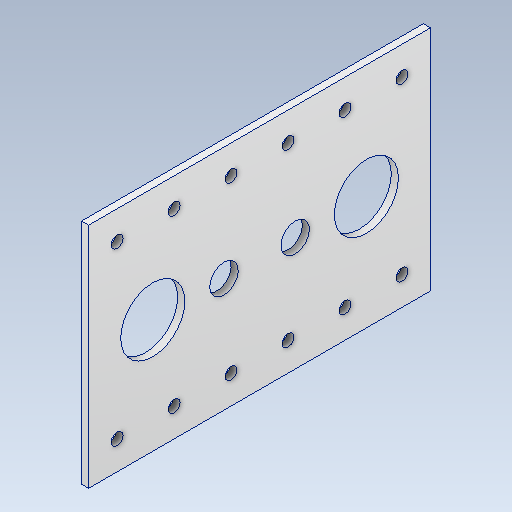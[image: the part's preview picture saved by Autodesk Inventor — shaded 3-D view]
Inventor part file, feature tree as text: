
AUTODESK INVENTOR PART (.ipt)
format: ipt  version: 2023 (Build 270158000, 158)  size: 138,240 bytes
history: native  units: in
note: dims shown in document units (in); Inventor stores cm internally (conversion verified against a paired STEP export)
features: other x3, sketch x1
ambient origin geometry x8: Origin, YZ Plane, XZ Plane, XY Plane, X Axis, Y Axis, Z Axis, Center Point
bodies: Solid1 (feature_tree)
feature tree (4):
  other  "CH-1-02-RearGearboxHousingMotorSide.ipt"
  other  "Solid1::CH-1-02-RearGearboxHousingMotorSide.ipt"
  other  "TaggingFeature1"
  sketch  "Sketch1"  dims[d0=0.3937in]
